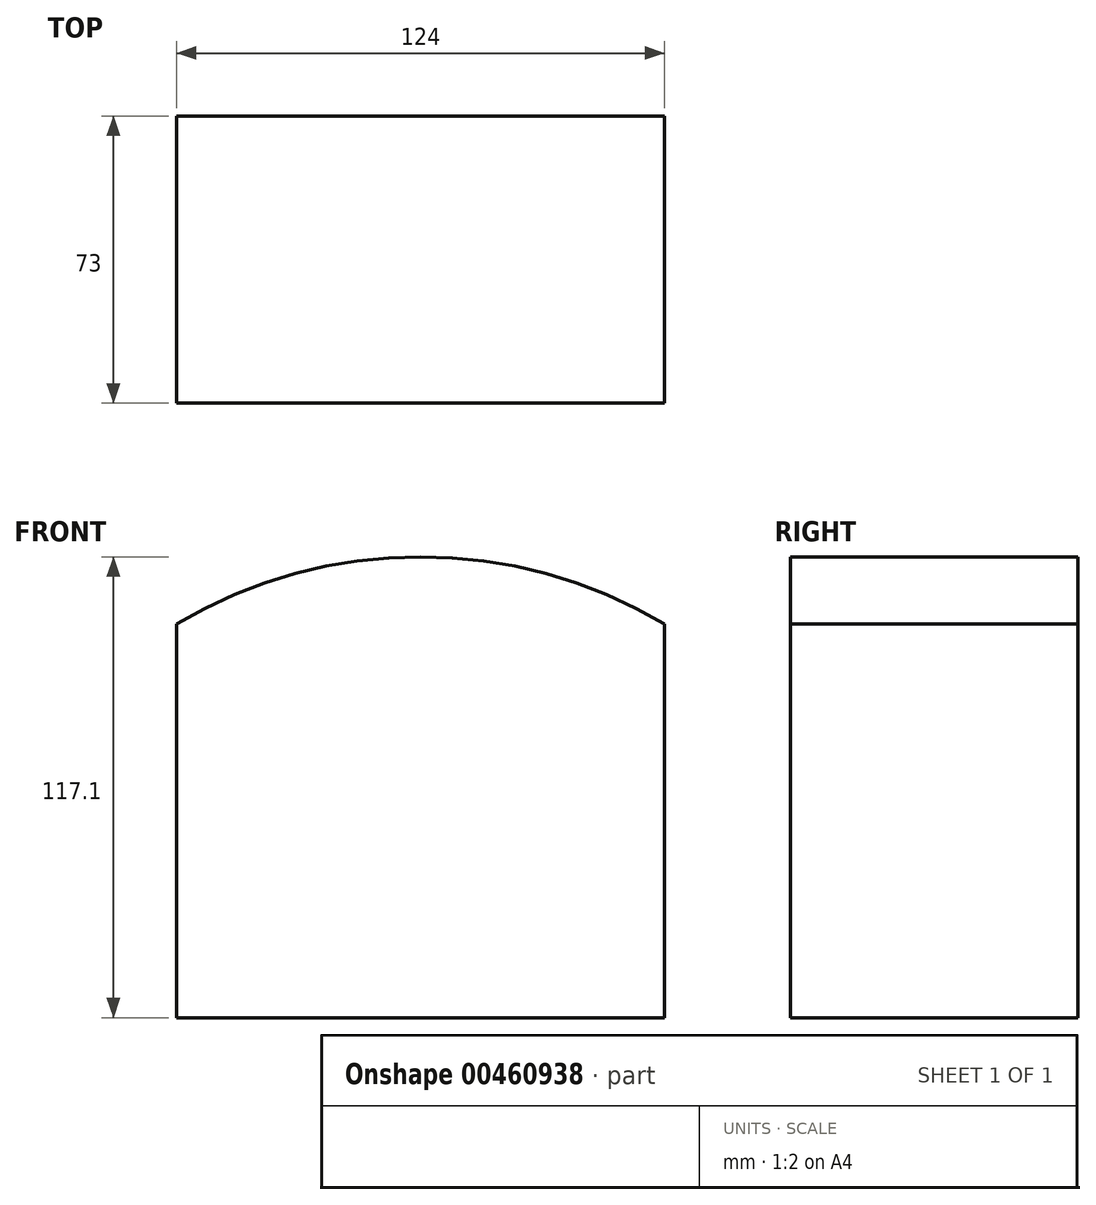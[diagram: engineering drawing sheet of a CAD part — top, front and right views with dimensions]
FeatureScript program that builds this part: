
annotation { "Feature Type Name" : "Feature", "Feature Type Description" : "" }
export const myFeature = defineFeature(function(context is Context, id is Id, definition is map)
    precondition{}
    {
        {
            var Q0;
            Q0=qCreatedBy(makeId("Front.planeOp"),FACE);
            var sketch = newSketch(context, id + "F0", { "sketchPlane" : qUnion([Q0])});
            skLineSegment(sketch, "E0", {"start": v(-62, 0) * mm, "end": v(62, 0) * mm});
            skLineSegment(sketch, "E1", {"start": v(62, 0) * mm, "end": v(62, 100) * mm});
            skLineSegment(sketch, "E2", {"start": v(-62, 0) * mm, "end": v(-62, 100) * mm});
            skArc(sketch, "E3", {"start": v(62, 100) * mm, "mid": v(0, 117.1) * mm, "end": v(-62, 100) * mm});
            skSolve(sketch);
        }
        {
            var Q0;
            Q0=makeQuery(id+"F0.imprint","IMPRINT",FACE,{"disambiguationData":[TD([[makeQuery(id+"F0.imprint","IMPRINT",EDGE,{"derivedFrom":sQuery(id+"F0.wireOp",EDGE,"E0")}),1.0]])]});
            extrude(context, id + "F1", {"entities" : qUnion([Q0]), "depth" : 73 * mm, "symmetric" : true});
        }
    });
